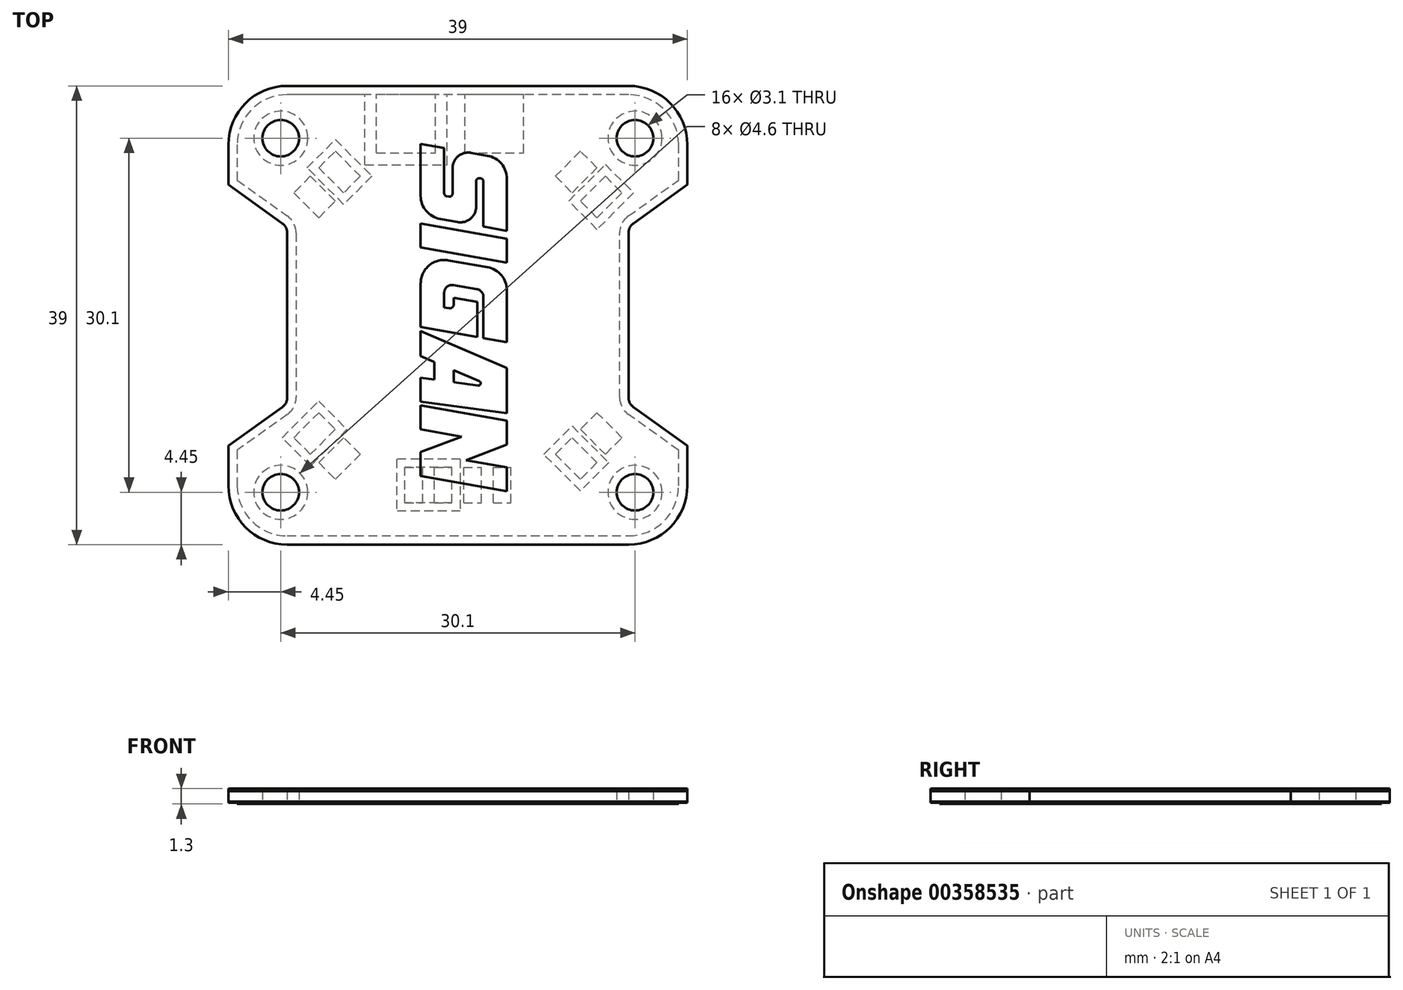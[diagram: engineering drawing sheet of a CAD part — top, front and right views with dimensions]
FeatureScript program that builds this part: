
annotation { "Feature Type Name" : "Feature", "Feature Type Description" : "" }
export const myFeature = defineFeature(function(context is Context, id is Id, definition is map)
    precondition{}
    {
        {
            var Q0;
            Q0=qCreatedBy(makeId("Top.planeOp"),FACE);
            var sketch = newSketch(context, id + "F0", { "sketchPlane" : qUnion([Q0])});
            skLineSegment(sketch, "E0.bottom", {"start": v(14.5, -19.5) * mm, "end": v(-14.5, -19.5) * mm});
            skLineSegment(sketch, "E0.top", {"start": v(14.5, 19.5) * mm, "end": v(7.5, 19.5) * mm});
            skLineSegment(sketch, "E0.left", {"start": v(19.5, -14.5) * mm, "end": v(19.5, -11.1) * mm});
            skLineSegment(sketch, "E0.right", {"start": v(-19.5, -14.5) * mm, "end": v(-19.5, -11.1) * mm});
            skPoint(sketch, "E0.middle", {"position": v(0, 0) * mm});
            skPoint(sketch, "E1.visualSharp", {"position": v(19.5, -19.5) * mm});
            skArc(sketch, "E1.filletArc", {"start": v(14.5, -19.5) * mm, "mid": v(18.04, -18.04) * mm, "end": v(19.5, -14.5) * mm});
            skPoint(sketch, "E2.visualSharp", {"position": v(-19.5, -19.5) * mm});
            skArc(sketch, "E2.filletArc", {"start": v(-19.5, -14.5) * mm, "mid": v(-18.04, -18.04) * mm, "end": v(-14.5, -19.5) * mm});
            skPoint(sketch, "E3.visualSharp", {"position": v(-19.5, 19.5) * mm});
            skArc(sketch, "E3.filletArc", {"start": v(-14.5, 19.5) * mm, "mid": v(-18.04, 18.04) * mm, "end": v(-19.5, 14.5) * mm});
            skPoint(sketch, "E4.visualSharp", {"position": v(19.5, 19.5) * mm});
            skArc(sketch, "E4.filletArc", {"start": v(19.5, 14.5) * mm, "mid": v(18.04, 18.04) * mm, "end": v(14.5, 19.5) * mm});
            skLineSegment(sketch, "E5", {"start": v(-7.5, 19.5) * mm, "end": v(-7.5, 19.5) * mm});
            skLineSegment(sketch, "E6", {"start": v(-7.5, 19.5) * mm, "end": v(7.5, 19.5) * mm});
            skLineSegment(sketch, "E7", {"start": v(7.5, 19.5) * mm, "end": v(7.5, 19.5) * mm});
            skLineSegment(sketch, "E8.trimOffspring", {"start": v(-7.5, 19.5) * mm, "end": v(-14.5, 19.5) * mm});
            skLineSegment(sketch, "E9", {"start": v(0, 19.5) * mm, "end": v(0, 0) * mm, "construction": true});
            skLineSegment(sketch, "E10.right", {"start": v(-14.5, 7) * mm, "end": v(-14.5, -7) * mm});
            skPoint(sketch, "E10.middle", {"position": v(-15.5, 0) * mm});
            skArc(sketch, "E11", {"start": v(-14.5, 7) * mm, "mid": v(-14.61, 7.46) * mm, "end": v(-14.92, 7.81) * mm});
            skArc(sketch, "E12", {"start": v(-14.92, -7.81) * mm, "mid": v(-14.61, -7.46) * mm, "end": v(-14.5, -7) * mm});
            skArc(sketch, "E13.MirrorCS", {"start": v(14.92, -7.81) * mm, "mid": v(14.61, -7.46) * mm, "end": v(14.5, -7) * mm});
            skArc(sketch, "E14.MirrorCS", {"start": v(14.5, 7) * mm, "mid": v(14.61, 7.46) * mm, "end": v(14.92, 7.81) * mm});
            skPoint(sketch, "E15.MirrorP", {"position": v(15.5, 0) * mm});
            skLineSegment(sketch, "E16.MirrorCS", {"start": v(14.5, 7) * mm, "end": v(14.5, -7) * mm});
            skCircle(sketch, "E17.0", {"center": v(-15.05, 15.05) * mm, "radius": 1.55 * mm});
            skCircle(sketch, "E17.1", {"center": v(15.05, 15.05) * mm, "radius": 1.55 * mm});
            skCircle(sketch, "E17.2", {"center": v(15.05, -15.05) * mm, "radius": 1.55 * mm});
            skCircle(sketch, "E17.3", {"center": v(-15.05, -15.05) * mm, "radius": 1.55 * mm});
            skLineSegment(sketch, "E18", {"start": v(14.92, -7.81) * mm, "end": v(19.5, -11.1) * mm});
            skLineSegment(sketch, "E19", {"start": v(0, 0) * mm, "end": v(26.56, 0) * mm, "construction": true});
            skLineSegment(sketch, "E20.MirrorCS", {"start": v(14.92, 7.81) * mm, "end": v(19.5, 11.1) * mm});
            skLineSegment(sketch, "E21.trimOffspring", {"start": v(19.5, 11.1) * mm, "end": v(19.5, 14.5) * mm});
            skPoint(sketch, "E22.orphan", {"position": v(16.5, 7) * mm});
            skPoint(sketch, "E23.MirrorCS.end.orphan", {"position": v(16.5, -7) * mm});
            skLineSegment(sketch, "E24.MirrorCS", {"start": v(-14.92, -7.81) * mm, "end": v(-19.5, -11.1) * mm});
            skLineSegment(sketch, "E25.MirrorCS", {"start": v(-14.92, 7.81) * mm, "end": v(-19.5, 11.1) * mm});
            skPoint(sketch, "E10.left.end.orphan", {"position": v(-16.5, -7) * mm});
            skPoint(sketch, "E26.orphan", {"position": v(-16.5, 7) * mm});
            skLineSegment(sketch, "E27.trimOffspring", {"start": v(-19.5, 11.1) * mm, "end": v(-19.5, 14.5) * mm});
            skSolve(sketch);
        }
        {
            var Q0;
            {var subQ0=makeQuery(id+"FaKBFoj8S7sMaQz_0.opExtrude","CAP_EDGE",EDGE,{"disambiguationData":[OSD([sQuery(id+"FUyg42RqR56omhc_0.wireOp",EDGE,"1f71cb04-1cd7-49c8-8af8-68a2ebdd6a70.filletArc")])],"isStart":true});Q0=makeQuery(id+"F0.imprint","IMPRINT",FACE,{"disambiguationData":[TD([[makeQuery(id+"F0.imprint","IMPRINT",EDGE,{"derivedFrom":subQ0}),-1.0]])]});}
            var Q1;
            Q1=makeQuery(id+"F0.imprint","IMPRINT",FACE,{"disambiguationData":[TD([[makeQuery(id+"F0.imprint","IMPRINT",EDGE,{"derivedFrom":sQuery(id+"F0.wireOp",EDGE,"E0.bottom")}),-1.0]])]});
            var Q2;
            {var subQ0=makeQuery(id+"FaKBFoj8S7sMaQz_0.opExtrude","CAP_EDGE",EDGE,{"disambiguationData":[OSD([sQuery(id+"FUyg42RqR56omhc_0.wireOp",EDGE,"45a09e78-3408-4181-94d1-7675ea45a7b5.0")])],"isStart":true});Q2=makeQuery(id+"F0.imprint","IMPRINT",FACE,{"disambiguationData":[TD([[makeQuery(id+"F0.imprint","IMPRINT",EDGE,{"derivedFrom":subQ0}),1.0]])]});}
            extrude(context, id + "F1", {"entities" : qUnion([Q0, Q1, Q2]), "depth" : 1 * mm});
        }
        {
            var Q0;
            Q0=makeQuery(id+"F1.opExtrude","SWEPT_BODY",BODY,{"disambiguationData":[OSD([sQuery(id+"FUyg42RqR56omhc_0.wireOp",EDGE,"apNCEg5n-BcgS-b9KA-570i-48yKU28l5lF8"),sQuery(id+"F0.wireOp",EDGE,"E0.bottom"),sQuery(id+"F0.wireOp",EDGE,"E0.top"),sQuery(id+"F0.wireOp",EDGE,"E0.left"),sQuery(id+"F0.wireOp",EDGE,"E0.right"),sQuery(id+"F0.wireOp",EDGE,"E1.filletArc"),sQuery(id+"F0.wireOp",EDGE,"E2.filletArc"),sQuery(id+"F0.wireOp",EDGE,"E3.filletArc"),sQuery(id+"F0.wireOp",EDGE,"E4.filletArc")])]});
            var Q1;
            Q1=qCreatedBy(makeId("Top.planeOp"),FACE);
            transform(context, id + "F2", {"entities" : qUnion([Q0]), "transformType" : TransformType.TRANSLATION_DISTANCE, "transformDirection" : qUnion([Q1]), "distance" : 6 * mm, "oppositeDirection" : true, "makeCopy" : false});
        }
        {
            var Q0;
            Q0=makeQuery(id+"F1.opExtrude","CAP_FACE",FACE,{"disambiguationData":[OSD([sQuery(id+"FUyg42RqR56omhc_0.wireOp",EDGE,"apNCEg5n-BcgS-b9KA-570i-48yKU28l5lF8"),sQuery(id+"F0.wireOp",EDGE,"E0.bottom"),sQuery(id+"F0.wireOp",EDGE,"E0.top"),sQuery(id+"F0.wireOp",EDGE,"E0.left"),sQuery(id+"F0.wireOp",EDGE,"E0.right"),sQuery(id+"F0.wireOp",EDGE,"E1.filletArc"),sQuery(id+"F0.wireOp",EDGE,"E2.filletArc"),sQuery(id+"F0.wireOp",EDGE,"E3.filletArc"),sQuery(id+"F0.wireOp",EDGE,"E4.filletArc"),sQuery(id+"F0.wireOp",EDGE,"E5"),sQuery(id+"F0.wireOp",EDGE,"E6"),sQuery(id+"F0.wireOp",EDGE,"E7"),sQuery(id+"F0.wireOp",EDGE,"E8.trimOffspring"),sQuery(id+"F0.wireOp",EDGE,"E10.left"),sQuery(id+"F0.wireOp",EDGE,"E10.right"),sQuery(id+"F0.wireOp",EDGE,"E11"),sQuery(id+"F0.wireOp",EDGE,"E12"),sQuery(id+"F0.wireOp",EDGE,"E13.MirrorCS"),sQuery(id+"F0.wireOp",EDGE,"E14.MirrorCS"),sQuery(id+"F0.wireOp",EDGE,"E23.MirrorCS"),sQuery(id+"F0.wireOp",EDGE,"E16.MirrorCS")])],"isStart":true});
            var sketch = newSketch(context, id + "F3", { "sketchPlane" : qUnion([Q0])});
            skLineSegment(sketch, "E28.bottom", {"start": v(0.6, -13.8) * mm, "end": v(5.6, -13.8) * mm});
            skLineSegment(sketch, "E28.top", {"start": v(0.6, -18.8) * mm, "end": v(5.6, -18.8) * mm});
            skLineSegment(sketch, "E28.left", {"start": v(0.6, -13.8) * mm, "end": v(0.6, -18.8) * mm});
            skLineSegment(sketch, "E28.right", {"start": v(5.6, -13.8) * mm, "end": v(5.6, -18.8) * mm});
            skPoint(sketch, "E28.middle", {"position": v(3.1, -16.3) * mm});
            skLineSegment(sketch, "E29.1.0.0", {"start": v(-1.9, -13.8) * mm, "end": v(-1.9, -18.8) * mm});
            skLineSegment(sketch, "E29.1.0.1", {"start": v(-6.9, -13.8) * mm, "end": v(-1.9, -13.8) * mm});
            skLineSegment(sketch, "E29.1.0.2", {"start": v(-6.9, -18.8) * mm, "end": v(-1.9, -18.8) * mm});
            skLineSegment(sketch, "E29.1.0.3", {"start": v(-6.9, -13.8) * mm, "end": v(-6.9, -18.8) * mm});
            skPoint(sketch, "E29.1.0.4", {"position": v(-4.4, -16.3) * mm});
            skLineSegment(sketch, "E29.direction1", {"start": v(0.6, -18.8) * mm, "end": v(-6.9, -18.8) * mm, "construction": true});
            skLineSegment(sketch, "E30", {"start": v(13.95, -10.41) * mm, "end": v(11.83, -8.29) * mm});
            skLineSegment(sketch, "E31", {"start": v(11.83, -8.29) * mm, "end": v(10.41, -9.7) * mm});
            skLineSegment(sketch, "E32", {"start": v(10.41, -9.7) * mm, "end": v(12.53, -11.83) * mm});
            skLineSegment(sketch, "E33", {"start": v(12.53, -11.83) * mm, "end": v(13.95, -10.41) * mm});
            skPoint(sketch, "E34.center", {"position": v(0, 0) * mm});
            skLineSegment(sketch, "E35", {"start": v(0, 0) * mm, "end": v(0, -24.64) * mm, "construction": true});
            skLineSegment(sketch, "E36", {"start": v(0, 0) * mm, "end": v(21.38, -21.38) * mm, "construction": true});
            skLineSegment(sketch, "E37.MirrorCS", {"start": v(8.29, -11.83) * mm, "end": v(9.7, -10.41) * mm});
            skLineSegment(sketch, "E38.MirrorCS", {"start": v(9.7, -10.41) * mm, "end": v(11.83, -12.53) * mm});
            skLineSegment(sketch, "E39.MirrorCS", {"start": v(10.41, -13.95) * mm, "end": v(8.29, -11.83) * mm});
            skLineSegment(sketch, "E40.MirrorCS", {"start": v(11.83, -12.53) * mm, "end": v(10.41, -13.95) * mm});
            skLineSegment(sketch, "E41.1.0", {"start": v(-8.29, -11.83) * mm, "end": v(-9.7, -10.41) * mm});
            skLineSegment(sketch, "E41.1.1", {"start": v(-11.83, -8.29) * mm, "end": v(-10.41, -9.7) * mm});
            skLineSegment(sketch, "E41.1.2", {"start": v(-10.41, -9.7) * mm, "end": v(-12.53, -11.83) * mm});
            skLineSegment(sketch, "E41.1.3", {"start": v(-9.7, -10.41) * mm, "end": v(-11.83, -12.53) * mm});
            skLineSegment(sketch, "E41.1.4", {"start": v(-11.83, -12.53) * mm, "end": v(-10.41, -13.95) * mm});
            skLineSegment(sketch, "E41.1.5", {"start": v(-12.53, -11.83) * mm, "end": v(-13.95, -10.41) * mm});
            skLineSegment(sketch, "E41.1.6", {"start": v(-10.41, -13.95) * mm, "end": v(-8.29, -11.83) * mm});
            skLineSegment(sketch, "E41.1.7", {"start": v(-13.95, -10.41) * mm, "end": v(-11.83, -8.29) * mm});
            skLineSegment(sketch, "E41.2.0", {"start": v(-11.83, 8.29) * mm, "end": v(-10.41, 9.7) * mm});
            skLineSegment(sketch, "E41.2.1", {"start": v(-8.29, 11.83) * mm, "end": v(-9.7, 10.41) * mm});
            skLineSegment(sketch, "E41.2.2", {"start": v(-9.7, 10.41) * mm, "end": v(-11.83, 12.53) * mm});
            skLineSegment(sketch, "E41.2.3", {"start": v(-10.41, 9.7) * mm, "end": v(-12.53, 11.83) * mm});
            skLineSegment(sketch, "E41.2.4", {"start": v(-12.53, 11.83) * mm, "end": v(-13.95, 10.41) * mm});
            skLineSegment(sketch, "E41.2.5", {"start": v(-11.83, 12.53) * mm, "end": v(-10.41, 13.95) * mm});
            skLineSegment(sketch, "E41.2.6", {"start": v(-13.95, 10.41) * mm, "end": v(-11.83, 8.29) * mm});
            skLineSegment(sketch, "E41.2.7", {"start": v(-10.41, 13.95) * mm, "end": v(-8.29, 11.83) * mm});
            skLineSegment(sketch, "E41.3.0", {"start": v(8.29, 11.83) * mm, "end": v(9.7, 10.41) * mm});
            skLineSegment(sketch, "E41.3.1", {"start": v(11.83, 8.29) * mm, "end": v(10.41, 9.7) * mm});
            skLineSegment(sketch, "E41.3.2", {"start": v(10.41, 9.7) * mm, "end": v(12.53, 11.83) * mm});
            skLineSegment(sketch, "E41.3.3", {"start": v(9.7, 10.41) * mm, "end": v(11.83, 12.53) * mm});
            skLineSegment(sketch, "E41.3.4", {"start": v(11.83, 12.53) * mm, "end": v(10.41, 13.95) * mm});
            skLineSegment(sketch, "E41.3.5", {"start": v(12.53, 11.83) * mm, "end": v(13.95, 10.41) * mm});
            skLineSegment(sketch, "E41.3.6", {"start": v(10.41, 13.95) * mm, "end": v(8.29, 11.83) * mm});
            skLineSegment(sketch, "E41.3.7", {"start": v(13.95, 10.41) * mm, "end": v(11.83, 8.29) * mm});
            skLineSegment(sketch, "E41.anchor1", {"start": v(0, 0) * mm, "end": v(10.41, -13.95) * mm, "construction": true});
            skLineSegment(sketch, "E41.anchor2", {"start": v(0, 0) * mm, "end": v(13.95, 10.41) * mm, "construction": true});
            skLineSegment(sketch, "E42.bottom", {"start": v(3, 15.94) * mm, "end": v(4.5, 15.94) * mm});
            skLineSegment(sketch, "E42.top", {"start": v(3, 12.94) * mm, "end": v(4.5, 12.94) * mm});
            skLineSegment(sketch, "E42.left", {"start": v(3, 15.94) * mm, "end": v(3, 12.94) * mm});
            skLineSegment(sketch, "E42.right", {"start": v(4.5, 15.94) * mm, "end": v(4.5, 12.94) * mm});
            skPoint(sketch, "E42.middle", {"position": v(3.75, 14.44) * mm});
            skPoint(sketch, "E43.1.0.0", {"position": v(1.25, 14.44) * mm});
            skLineSegment(sketch, "E43.1.0.1", {"start": v(0.5, 12.94) * mm, "end": v(2, 12.94) * mm});
            skLineSegment(sketch, "E43.1.0.2", {"start": v(2, 15.94) * mm, "end": v(2, 12.94) * mm});
            skLineSegment(sketch, "E43.1.0.3", {"start": v(0.5, 15.94) * mm, "end": v(0.5, 12.94) * mm});
            skLineSegment(sketch, "E43.1.0.4", {"start": v(0.5, 15.94) * mm, "end": v(2, 15.94) * mm});
            skPoint(sketch, "E43.2.0.0", {"position": v(-1.25, 14.44) * mm});
            skLineSegment(sketch, "E43.2.0.1", {"start": v(-2, 12.94) * mm, "end": v(-0.5, 12.94) * mm});
            skLineSegment(sketch, "E43.2.0.2", {"start": v(-0.5, 15.94) * mm, "end": v(-0.5, 12.94) * mm});
            skLineSegment(sketch, "E43.2.0.3", {"start": v(-2, 15.94) * mm, "end": v(-2, 12.94) * mm});
            skLineSegment(sketch, "E43.2.0.4", {"start": v(-2, 15.94) * mm, "end": v(-0.5, 15.94) * mm});
            skPoint(sketch, "E43.3.0.0", {"position": v(-3.75, 14.44) * mm});
            skLineSegment(sketch, "E43.3.0.1", {"start": v(-4.5, 12.94) * mm, "end": v(-3, 12.94) * mm});
            skLineSegment(sketch, "E43.3.0.2", {"start": v(-3, 15.94) * mm, "end": v(-3, 12.94) * mm});
            skLineSegment(sketch, "E43.3.0.3", {"start": v(-4.5, 15.94) * mm, "end": v(-4.5, 12.94) * mm});
            skLineSegment(sketch, "E43.3.0.4", {"start": v(-4.5, 15.94) * mm, "end": v(-3, 15.94) * mm});
            skLineSegment(sketch, "E43.direction1", {"start": v(3, 12.94) * mm, "end": v(0.5, 12.94) * mm, "construction": true});
            skSolve(sketch);
        }
        {
            var Q0;
            Q0=makeQuery(id+"F3.imprint","IMPRINT",FACE,{"disambiguationData":[TD([[makeQuery(id+"F3.imprint","IMPRINT",EDGE,{"derivedFrom":sQuery(id+"F3.wireOp",EDGE,"E28.bottom")}),1.0]])]});
            extrude(context, id + "F4", {"entities" : qUnion([Q0]), "depth" : .1 * mm});
        }
        {
            var Q0;
            Q0=makeQuery(id+"F1.opExtrude","CAP_FACE",FACE,{"disambiguationData":[OSD([sQuery(id+"FUyg42RqR56omhc_0.wireOp",EDGE,"apNCEg5n-BcgS-b9KA-570i-48yKU28l5lF8"),sQuery(id+"F0.wireOp",EDGE,"E0.bottom"),sQuery(id+"F0.wireOp",EDGE,"E0.top"),sQuery(id+"F0.wireOp",EDGE,"E0.left"),sQuery(id+"F0.wireOp",EDGE,"E0.right"),sQuery(id+"F0.wireOp",EDGE,"E1.filletArc"),sQuery(id+"F0.wireOp",EDGE,"E2.filletArc"),sQuery(id+"F0.wireOp",EDGE,"E3.filletArc"),sQuery(id+"F0.wireOp",EDGE,"E4.filletArc"),sQuery(id+"F0.wireOp",EDGE,"E5"),sQuery(id+"F0.wireOp",EDGE,"E6"),sQuery(id+"F0.wireOp",EDGE,"E7"),sQuery(id+"F0.wireOp",EDGE,"E8.trimOffspring"),sQuery(id+"F0.wireOp",EDGE,"E10.left"),sQuery(id+"F0.wireOp",EDGE,"E10.right"),sQuery(id+"F0.wireOp",EDGE,"E11"),sQuery(id+"F0.wireOp",EDGE,"E12"),sQuery(id+"F0.wireOp",EDGE,"E13.MirrorCS"),sQuery(id+"F0.wireOp",EDGE,"E14.MirrorCS"),sQuery(id+"F0.wireOp",EDGE,"E23.MirrorCS"),sQuery(id+"F0.wireOp",EDGE,"E16.MirrorCS")])],"isStart":true});
            var sketch = newSketch(context, id + "F5", { "sketchPlane" : qUnion([Q0])});
            skLineSegment(sketch, "E44.0", {"start": v(9.42, -9.7) * mm, "end": v(12.53, -12.82) * mm});
            skLineSegment(sketch, "E44.1", {"start": v(11.83, -7.3) * mm, "end": v(9.42, -9.7) * mm});
            skLineSegment(sketch, "E44.2", {"start": v(14.94, -10.41) * mm, "end": v(11.83, -7.3) * mm});
            skLineSegment(sketch, "E44.3", {"start": v(12.53, -12.82) * mm, "end": v(14.94, -10.41) * mm});
            skLineSegment(sketch, "E45.1.0", {"start": v(7.3, 11.83) * mm, "end": v(9.7, 9.42) * mm});
            skLineSegment(sketch, "E45.1.1", {"start": v(9.7, 9.42) * mm, "end": v(12.82, 12.53) * mm});
            skLineSegment(sketch, "E45.1.2", {"start": v(10.41, 14.94) * mm, "end": v(7.3, 11.83) * mm});
            skLineSegment(sketch, "E45.1.3", {"start": v(12.82, 12.53) * mm, "end": v(10.41, 14.94) * mm});
            skLineSegment(sketch, "E45.2.0", {"start": v(-11.83, 7.3) * mm, "end": v(-9.42, 9.7) * mm});
            skLineSegment(sketch, "E45.2.1", {"start": v(-9.42, 9.7) * mm, "end": v(-12.53, 12.82) * mm});
            skLineSegment(sketch, "E45.2.2", {"start": v(-14.94, 10.41) * mm, "end": v(-11.83, 7.3) * mm});
            skLineSegment(sketch, "E45.2.3", {"start": v(-12.53, 12.82) * mm, "end": v(-14.94, 10.41) * mm});
            skLineSegment(sketch, "E45.3.0", {"start": v(-7.3, -11.83) * mm, "end": v(-9.7, -9.42) * mm});
            skLineSegment(sketch, "E45.3.1", {"start": v(-9.7, -9.42) * mm, "end": v(-12.82, -12.53) * mm});
            skLineSegment(sketch, "E45.3.2", {"start": v(-10.41, -14.94) * mm, "end": v(-7.9, -12.43) * mm});
            skLineSegment(sketch, "E45.3.3", {"start": v(-12.82, -12.53) * mm, "end": v(-10.41, -14.94) * mm});
            skPoint(sketch, "E45.center", {"position": v(0, 0) * mm});
            skLineSegment(sketch, "E46.0", {"start": v(-0.9, -12.8) * mm, "end": v(-0.9, -19.5) * mm});
            skLineSegment(sketch, "E46.1", {"start": v(-7.9, -12.8) * mm, "end": v(-0.9, -12.8) * mm});
            skLineSegment(sketch, "E46.2", {"start": v(-7.9, -12.8) * mm, "end": v(-7.9, -19.5) * mm});
            skLineSegment(sketch, "E47.0", {"start": v(14.5, -19.5) * mm, "end": v(-14.5, -19.5) * mm});
            skLineSegment(sketch, "E48.trimOffspring", {"start": v(-7.9, -12.43) * mm, "end": v(-7.3, -11.83) * mm});
            skArc(sketch, "E49.0", {"start": v(18.75, -14.5) * mm, "mid": v(17.5, -17.5) * mm, "end": v(14.5, -18.75) * mm});
            skLineSegment(sketch, "E49.1", {"start": v(18.75, 14.5) * mm, "end": v(18.75, 11.48) * mm});
            skLineSegment(sketch, "E49.2", {"start": v(14.5, -18.75) * mm, "end": v(-14.5, -18.75) * mm});
            skArc(sketch, "E49.3", {"start": v(14.5, 18.75) * mm, "mid": v(17.5, 17.5) * mm, "end": v(18.75, 14.5) * mm});
            skArc(sketch, "E49.4", {"start": v(-14.5, -18.75) * mm, "mid": v(-17.5, -17.5) * mm, "end": v(-18.75, -14.5) * mm});
            skLineSegment(sketch, "E49.5", {"start": v(-18.75, 14.5) * mm, "end": v(-18.75, 11.48) * mm});
            skArc(sketch, "E49.6", {"start": v(-18.75, 14.5) * mm, "mid": v(-17.5, 17.5) * mm, "end": v(-14.5, 18.75) * mm});
            skLineSegment(sketch, "E49.7", {"start": v(14.5, 18.75) * mm, "end": v(-14.5, 18.75) * mm});
            skCircle(sketch, "E50.0", {"center": v(15.05, -15.05) * mm, "radius": 2.3 * mm});
            skCircle(sketch, "E51.0", {"center": v(-15.05, -15.05) * mm, "radius": 2.3 * mm});
            skCircle(sketch, "E52.0", {"center": v(-15.05, 15.05) * mm, "radius": 2.3 * mm});
            skCircle(sketch, "E53.0", {"center": v(15.05, 15.05) * mm, "radius": 2.3 * mm});
            skLineSegment(sketch, "E54.0", {"start": v(10.41, -9.7) * mm, "end": v(12.53, -11.83) * mm});
            skLineSegment(sketch, "E54.1", {"start": v(12.53, -11.83) * mm, "end": v(13.95, -10.41) * mm});
            skLineSegment(sketch, "E54.2", {"start": v(13.95, -10.41) * mm, "end": v(11.83, -8.29) * mm});
            skLineSegment(sketch, "E54.3", {"start": v(11.83, -8.29) * mm, "end": v(10.41, -9.7) * mm});
            skLineSegment(sketch, "E54.4", {"start": v(-10.41, -13.95) * mm, "end": v(-8.29, -11.83) * mm});
            skLineSegment(sketch, "E54.5", {"start": v(-11.83, -12.53) * mm, "end": v(-10.41, -13.95) * mm});
            skLineSegment(sketch, "E54.6", {"start": v(-9.7, -10.41) * mm, "end": v(-11.83, -12.53) * mm});
            skLineSegment(sketch, "E54.7", {"start": v(-8.29, -11.83) * mm, "end": v(-9.7, -10.41) * mm});
            skLineSegment(sketch, "E54.8", {"start": v(-13.95, 10.41) * mm, "end": v(-11.83, 8.29) * mm});
            skLineSegment(sketch, "E54.9", {"start": v(-11.83, 8.29) * mm, "end": v(-10.41, 9.7) * mm});
            skLineSegment(sketch, "E54.10", {"start": v(-12.53, 11.83) * mm, "end": v(-13.95, 10.41) * mm});
            skLineSegment(sketch, "E54.11", {"start": v(-10.41, 9.7) * mm, "end": v(-12.53, 11.83) * mm});
            skLineSegment(sketch, "E54.12", {"start": v(9.7, 10.41) * mm, "end": v(11.83, 12.53) * mm});
            skLineSegment(sketch, "E54.13", {"start": v(8.29, 11.83) * mm, "end": v(9.7, 10.41) * mm});
            skLineSegment(sketch, "E54.14", {"start": v(10.41, 13.95) * mm, "end": v(8.29, 11.83) * mm});
            skLineSegment(sketch, "E54.15", {"start": v(11.83, 12.53) * mm, "end": v(10.41, 13.95) * mm});
            skLineSegment(sketch, "E55.0", {"start": v(-1.9, -13.8) * mm, "end": v(-1.9, -18.8) * mm});
            skLineSegment(sketch, "E55.1", {"start": v(-6.9, -13.8) * mm, "end": v(-1.9, -13.8) * mm});
            skLineSegment(sketch, "E55.2", {"start": v(-6.9, -13.8) * mm, "end": v(-6.9, -18.8) * mm});
            skLineSegment(sketch, "E55.3", {"start": v(-6.9, -18.8) * mm, "end": v(-1.9, -18.8) * mm});
            skLineSegment(sketch, "E56.bottom", {"start": v(0.2, 12.24) * mm, "end": v(-5.2, 12.24) * mm});
            skLineSegment(sketch, "E56.top", {"start": v(0.2, 16.64) * mm, "end": v(-5.2, 16.64) * mm});
            skLineSegment(sketch, "E56.left", {"start": v(0.2, 12.24) * mm, "end": v(0.2, 16.64) * mm});
            skLineSegment(sketch, "E56.right", {"start": v(-5.2, 12.24) * mm, "end": v(-5.2, 16.64) * mm});
            skLineSegment(sketch, "E57.bottom", {"start": v(-0.5, 12.94) * mm, "end": v(-4.5, 12.94) * mm});
            skLineSegment(sketch, "E57.top", {"start": v(-0.5, 15.94) * mm, "end": v(-4.5, 15.94) * mm});
            skLineSegment(sketch, "E57.left", {"start": v(-0.5, 12.94) * mm, "end": v(-0.5, 15.94) * mm});
            skLineSegment(sketch, "E57.right", {"start": v(-4.5, 12.94) * mm, "end": v(-4.5, 15.94) * mm});
            skLineSegment(sketch, "E58.0", {"start": v(-14.48, 8.42) * mm, "end": v(-18.75, 11.48) * mm});
            skLineSegment(sketch, "E58.1", {"start": v(-14.48, -8.42) * mm, "end": v(-18.75, -11.48) * mm});
            skArc(sketch, "E58.2", {"start": v(-13.75, -7) * mm, "mid": v(-13.94, -7.8) * mm, "end": v(-14.48, -8.42) * mm});
            skLineSegment(sketch, "E58.3", {"start": v(-13.75, -7) * mm, "end": v(-13.75, 7) * mm});
            skArc(sketch, "E58.4", {"start": v(-14.48, 8.42) * mm, "mid": v(-13.94, 7.8) * mm, "end": v(-13.75, 7) * mm});
            skLineSegment(sketch, "E59.trimOffspring", {"start": v(-18.75, -11.48) * mm, "end": v(-18.75, -14.5) * mm});
            skLineSegment(sketch, "E60.0", {"start": v(14.48, 8.42) * mm, "end": v(18.75, 11.48) * mm});
            skLineSegment(sketch, "E60.1", {"start": v(14.48, -8.42) * mm, "end": v(18.75, -11.48) * mm});
            skArc(sketch, "E60.2", {"start": v(13.75, -7) * mm, "mid": v(13.94, -7.8) * mm, "end": v(14.48, -8.42) * mm});
            skLineSegment(sketch, "E60.3", {"start": v(13.75, -7) * mm, "end": v(13.75, 7) * mm});
            skArc(sketch, "E60.4", {"start": v(14.48, 8.42) * mm, "mid": v(13.94, 7.8) * mm, "end": v(13.75, 7) * mm});
            skLineSegment(sketch, "E61.trimOffspring", {"start": v(18.75, -11.48) * mm, "end": v(18.75, -14.5) * mm});
            skSolve(sketch);
        }
        {
            var Q0;
            Q0=makeQuery(id+"F5.imprint","IMPRINT",FACE,{"disambiguationData":[TD([[makeQuery(id+"F5.imprint","IMPRINT",EDGE,{"derivedFrom":sQuery(id+"F5.wireOp",EDGE,"E44.0")}),-1.0]])]});
            var Q1;
            Q1=makeQuery(id+"F5.imprint","IMPRINT",FACE,{"disambiguationData":[TD([[makeQuery(id+"F5.imprint","IMPRINT",EDGE,{"derivedFrom":sQuery(id+"F5.wireOp",EDGE,"E54.0")}),1.0]])]});
            var Q2;
            Q2=makeQuery(id+"F5.imprint","IMPRINT",FACE,{"disambiguationData":[TD([[makeQuery(id+"F5.imprint","IMPRINT",EDGE,{"derivedFrom":sQuery(id+"F5.wireOp",EDGE,"E54.4")}),1.0]])]});
            var Q3;
            Q3=makeQuery(id+"F5.imprint","IMPRINT",FACE,{"disambiguationData":[TD([[makeQuery(id+"F5.imprint","IMPRINT",EDGE,{"derivedFrom":sQuery(id+"F5.wireOp",EDGE,"E54.8")}),1.0]])]});
            var Q4;
            Q4=makeQuery(id+"F5.imprint","IMPRINT",FACE,{"disambiguationData":[TD([[makeQuery(id+"F5.imprint","IMPRINT",EDGE,{"derivedFrom":sQuery(id+"F5.wireOp",EDGE,"E54.12")}),1.0]])]});
            var Q5;
            {var subQ5=sQuery(id+"F5.wireOp",EDGE,"E55.1");Q5=makeQuery(id+"F5.imprint","IMPRINT",FACE,{"disambiguationData":[TD([[makeQuery(id+"F5.imprint","IMPRINT",EDGE,{"derivedFrom":subQ5}),-1.0]])]});}
            var Q6;
            Q6=makeQuery(id+"F5.imprint","IMPRINT",FACE,{"disambiguationData":[TD([[makeQuery(id+"F5.imprint","IMPRINT",EDGE,{"derivedFrom":sQuery(id+"F5.wireOp",EDGE,"E57.bottom")}),-1.0]])]});
            extrude(context, id + "F6", {"entities" : qUnion([Q0, Q1, Q2, Q3, Q4, Q5, Q6]), "depth" : .1 * mm});
        }
        {
            var Q0;
            Q0=makeQuery(id+"F4.opExtrude","SWEPT_BODY",BODY,{"disambiguationData":[OSD([sQuery(id+"FUyg42RqR56omhc_0.wireOp",EDGE,"apNCEg5n-BcgS-b9KA-570i-48yKU28l5lF8"),sQuery(id+"F0.wireOp",EDGE,"E0.bottom"),sQuery(id+"F0.wireOp",EDGE,"E0.top"),sQuery(id+"F0.wireOp",EDGE,"E0.left"),sQuery(id+"F0.wireOp",EDGE,"E0.right"),sQuery(id+"F0.wireOp",EDGE,"E1.filletArc"),sQuery(id+"F0.wireOp",EDGE,"E2.filletArc"),sQuery(id+"F0.wireOp",EDGE,"E3.filletArc"),sQuery(id+"F0.wireOp",EDGE,"E4.filletArc"),sQuery(id+"F0.wireOp",EDGE,"E5"),sQuery(id+"F0.wireOp",EDGE,"E6"),sQuery(id+"F0.wireOp",EDGE,"E7"),sQuery(id+"F0.wireOp",EDGE,"E8.trimOffspring"),sQuery(id+"F0.wireOp",EDGE,"E10.left"),sQuery(id+"F0.wireOp",EDGE,"E10.right"),sQuery(id+"F0.wireOp",EDGE,"E11"),sQuery(id+"F0.wireOp",EDGE,"E12"),sQuery(id+"F0.wireOp",EDGE,"E13.MirrorCS"),sQuery(id+"F0.wireOp",EDGE,"E14.MirrorCS"),sQuery(id+"F0.wireOp",EDGE,"E23.MirrorCS"),sQuery(id+"F0.wireOp",EDGE,"E16.MirrorCS"),sQuery(id+"F3.wireOp",EDGE,"E28.bottom"),sQuery(id+"F3.wireOp",EDGE,"E28.top"),sQuery(id+"F3.wireOp",EDGE,"E28.left"),sQuery(id+"F3.wireOp",EDGE,"E28.right"),sQuery(id+"F3.wireOp",EDGE,"E29.1.0.0"),sQuery(id+"F3.wireOp",EDGE,"E29.1.0.1"),sQuery(id+"F3.wireOp",EDGE,"E29.1.0.2"),sQuery(id+"F3.wireOp",EDGE,"E29.1.0.3"),sQuery(id+"F3.wireOp",EDGE,"E30"),sQuery(id+"F3.wireOp",EDGE,"E31"),sQuery(id+"F3.wireOp",EDGE,"E32"),sQuery(id+"F3.wireOp",EDGE,"E33"),sQuery(id+"F3.wireOp",EDGE,"E37.MirrorCS"),sQuery(id+"F3.wireOp",EDGE,"E38.MirrorCS"),sQuery(id+"F3.wireOp",EDGE,"E39.MirrorCS"),sQuery(id+"F3.wireOp",EDGE,"E40.MirrorCS"),sQuery(id+"F3.wireOp",EDGE,"E41.1.0"),sQuery(id+"F3.wireOp",EDGE,"E41.1.1"),sQuery(id+"F3.wireOp",EDGE,"E41.1.2"),sQuery(id+"F3.wireOp",EDGE,"E41.1.3"),sQuery(id+"F3.wireOp",EDGE,"E41.1.4"),sQuery(id+"F3.wireOp",EDGE,"E41.1.5"),sQuery(id+"F3.wireOp",EDGE,"E41.1.6"),sQuery(id+"F3.wireOp",EDGE,"E41.1.7"),sQuery(id+"F3.wireOp",EDGE,"E41.2.0"),sQuery(id+"F3.wireOp",EDGE,"E41.2.1"),sQuery(id+"F3.wireOp",EDGE,"E41.2.2"),sQuery(id+"F3.wireOp",EDGE,"E41.2.3"),sQuery(id+"F3.wireOp",EDGE,"E41.2.4"),sQuery(id+"F3.wireOp",EDGE,"E41.2.5"),sQuery(id+"F3.wireOp",EDGE,"E41.2.6"),sQuery(id+"F3.wireOp",EDGE,"E41.2.7"),sQuery(id+"F3.wireOp",EDGE,"E41.3.0"),sQuery(id+"F3.wireOp",EDGE,"E41.3.1"),sQuery(id+"F3.wireOp",EDGE,"E41.3.2"),sQuery(id+"F3.wireOp",EDGE,"E41.3.3"),sQuery(id+"F3.wireOp",EDGE,"E41.3.4"),sQuery(id+"F3.wireOp",EDGE,"E41.3.5"),sQuery(id+"F3.wireOp",EDGE,"E41.3.6"),sQuery(id+"F3.wireOp",EDGE,"E41.3.7"),sQuery(id+"F3.wireOp",EDGE,"E42.bottom"),sQuery(id+"F3.wireOp",EDGE,"E42.top"),sQuery(id+"F3.wireOp",EDGE,"E42.left"),sQuery(id+"F3.wireOp",EDGE,"E42.right"),sQuery(id+"F3.wireOp",EDGE,"E43.1.0.1"),sQuery(id+"F3.wireOp",EDGE,"E43.1.0.2"),sQuery(id+"F3.wireOp",EDGE,"E43.1.0.3"),sQuery(id+"F3.wireOp",EDGE,"E43.1.0.4"),sQuery(id+"F3.wireOp",EDGE,"E43.2.0.1"),sQuery(id+"F3.wireOp",EDGE,"E43.2.0.2"),sQuery(id+"F3.wireOp",EDGE,"E43.2.0.3"),sQuery(id+"F3.wireOp",EDGE,"E43.2.0.4"),sQuery(id+"F3.wireOp",EDGE,"E43.3.0.1"),sQuery(id+"F3.wireOp",EDGE,"E43.3.0.2"),sQuery(id+"F3.wireOp",EDGE,"E43.3.0.3"),sQuery(id+"F3.wireOp",EDGE,"E43.3.0.4")])]});
            var Q1;
            Q1=qCreatedBy(makeId("Top.planeOp"),FACE);
            transform(context, id + "F7", {"entities" : qUnion([Q0]), "transformType" : TransformType.TRANSLATION_DISTANCE, "transformDirection" : qUnion([Q1]), "distance" : .1 * mm, "makeCopy" : false});
        }
        {
            var Q0;
            Q0=makeQuery(id+"F1.opExtrude","CAP_FACE",FACE,{"disambiguationData":[OSD([sQuery(id+"FUyg42RqR56omhc_0.wireOp",EDGE,"apNCEg5n-BcgS-b9KA-570i-48yKU28l5lF8"),sQuery(id+"F0.wireOp",EDGE,"E0.bottom"),sQuery(id+"F0.wireOp",EDGE,"E0.top"),sQuery(id+"F0.wireOp",EDGE,"E0.left"),sQuery(id+"F0.wireOp",EDGE,"E0.right"),sQuery(id+"F0.wireOp",EDGE,"E1.filletArc"),sQuery(id+"F0.wireOp",EDGE,"E2.filletArc"),sQuery(id+"F0.wireOp",EDGE,"E3.filletArc"),sQuery(id+"F0.wireOp",EDGE,"E4.filletArc"),sQuery(id+"F0.wireOp",EDGE,"E6"),sQuery(id+"F0.wireOp",EDGE,"E8.trimOffspring"),sQuery(id+"F0.wireOp",EDGE,"E10.left"),sQuery(id+"F0.wireOp",EDGE,"E10.right"),sQuery(id+"F0.wireOp",EDGE,"E11"),sQuery(id+"F0.wireOp",EDGE,"E12"),sQuery(id+"F0.wireOp",EDGE,"E13.MirrorCS"),sQuery(id+"F0.wireOp",EDGE,"E14.MirrorCS"),sQuery(id+"F0.wireOp",EDGE,"E23.MirrorCS"),sQuery(id+"F0.wireOp",EDGE,"E16.MirrorCS")])],"isStart":false});
            var sketch = newSketch(context, id + "F8", { "sketchPlane" : qUnion([Q0])});
            skCircle(sketch, "E62.8", {"center": v(-15.05, -15.05) * mm, "radius": 2.3 * mm});
            skCircle(sketch, "E62.9", {"center": v(-15.05, 15.05) * mm, "radius": 2.3 * mm});
            skCircle(sketch, "E62.10", {"center": v(15.05, 15.05) * mm, "radius": 2.3 * mm});
            skCircle(sketch, "E62.11", {"center": v(15.05, -15.05) * mm, "radius": 2.3 * mm});
            skArc(sketch, "E63.0", {"start": v(18.75, 14.5) * mm, "mid": v(17.5, 17.5) * mm, "end": v(14.5, 18.75) * mm});
            skLineSegment(sketch, "E63.1", {"start": v(18.75, 11.48) * mm, "end": v(18.75, 14.5) * mm});
            skLineSegment(sketch, "E63.2", {"start": v(14.48, 8.42) * mm, "end": v(18.75, 11.48) * mm});
            skArc(sketch, "E63.3", {"start": v(13.75, 7) * mm, "mid": v(13.94, 7.8) * mm, "end": v(14.48, 8.42) * mm});
            skLineSegment(sketch, "E63.4", {"start": v(13.75, -7) * mm, "end": v(13.75, 7) * mm});
            skLineSegment(sketch, "E63.5", {"start": v(14.5, 18.75) * mm, "end": v(-14.5, 18.75) * mm});
            skArc(sketch, "E63.6", {"start": v(14.48, -8.42) * mm, "mid": v(13.94, -7.8) * mm, "end": v(13.75, -7) * mm});
            skLineSegment(sketch, "E63.7", {"start": v(18.75, -11.48) * mm, "end": v(14.48, -8.42) * mm});
            skLineSegment(sketch, "E63.8", {"start": v(18.75, -14.5) * mm, "end": v(18.75, -11.48) * mm});
            skArc(sketch, "E63.9", {"start": v(14.5, -18.75) * mm, "mid": v(17.5, -17.5) * mm, "end": v(18.75, -14.5) * mm});
            skArc(sketch, "E63.10", {"start": v(-14.48, 8.42) * mm, "mid": v(-13.94, 7.8) * mm, "end": v(-13.75, 7) * mm});
            skLineSegment(sketch, "E63.11", {"start": v(-18.75, 11.48) * mm, "end": v(-14.48, 8.42) * mm});
            skLineSegment(sketch, "E63.12", {"start": v(-18.75, 14.5) * mm, "end": v(-18.75, 11.48) * mm});
            skArc(sketch, "E63.13", {"start": v(-14.5, 18.75) * mm, "mid": v(-17.5, 17.5) * mm, "end": v(-18.75, 14.5) * mm});
            skLineSegment(sketch, "E63.14", {"start": v(-13.75, 7) * mm, "end": v(-13.75, -7) * mm});
            skArc(sketch, "E63.15", {"start": v(-13.75, -7) * mm, "mid": v(-13.94, -7.8) * mm, "end": v(-14.48, -8.42) * mm});
            skLineSegment(sketch, "E63.16", {"start": v(-14.48, -8.42) * mm, "end": v(-18.75, -11.48) * mm});
            skLineSegment(sketch, "E63.17", {"start": v(-18.75, -11.48) * mm, "end": v(-18.75, -14.5) * mm});
            skArc(sketch, "E63.18", {"start": v(-18.75, -14.5) * mm, "mid": v(-17.5, -17.5) * mm, "end": v(-14.5, -18.75) * mm});
            skLineSegment(sketch, "E63.19", {"start": v(-14.5, -18.75) * mm, "end": v(14.5, -18.75) * mm});
            skSolve(sketch);
        }
        {
            var Q0;
            Q0=qSketchRegion(id+"F8",true);
            extrude(context, id + "F9", {"entities" : qUnion([Q0]), "depth" : .1 * mm});
        }
        {
            var Q0;
            Q0=makeQuery(id+"F1.opExtrude","CAP_FACE",FACE,{"disambiguationData":[OSD([sQuery(id+"F0.wireOp",EDGE,"E0.bottom"),sQuery(id+"F0.wireOp",EDGE,"E0.top"),sQuery(id+"F0.wireOp",EDGE,"E0.left"),sQuery(id+"F0.wireOp",EDGE,"E0.right"),sQuery(id+"F0.wireOp",EDGE,"E1.filletArc"),sQuery(id+"F0.wireOp",EDGE,"E2.filletArc"),sQuery(id+"F0.wireOp",EDGE,"E3.filletArc"),sQuery(id+"F0.wireOp",EDGE,"E4.filletArc"),sQuery(id+"F0.wireOp",EDGE,"E6"),sQuery(id+"F0.wireOp",EDGE,"E8.trimOffspring"),sQuery(id+"F0.wireOp",EDGE,"E10.right"),sQuery(id+"F0.wireOp",EDGE,"E11"),sQuery(id+"F0.wireOp",EDGE,"E12"),sQuery(id+"F0.wireOp",EDGE,"E13.MirrorCS"),sQuery(id+"F0.wireOp",EDGE,"E14.MirrorCS"),sQuery(id+"F0.wireOp",EDGE,"E16.MirrorCS"),sQuery(id+"F0.wireOp",EDGE,"E17.0"),sQuery(id+"F0.wireOp",EDGE,"E17.1"),sQuery(id+"F0.wireOp",EDGE,"E17.2"),sQuery(id+"F0.wireOp",EDGE,"E17.3"),sQuery(id+"F0.wireOp",EDGE,"E18"),sQuery(id+"F0.wireOp",EDGE,"E20.MirrorCS"),sQuery(id+"F0.wireOp",EDGE,"E21.trimOffspring"),sQuery(id+"F0.wireOp",EDGE,"E24.MirrorCS"),sQuery(id+"F0.wireOp",EDGE,"E25.MirrorCS"),sQuery(id+"F0.wireOp",EDGE,"E27.trimOffspring")])],"isStart":false});
            extrude(context, id + "F10", {"entities" : qUnion([Q0]), "depth" : .1 * mm});
        }
        {
            var Q0;
            Q0=makeQuery(id+"F10.opExtrude","CAP_FACE",FACE,{"disambiguationData":[OSD([sQuery(id+"F0.wireOp",EDGE,"E0.bottom"),sQuery(id+"F0.wireOp",EDGE,"E0.top"),sQuery(id+"F0.wireOp",EDGE,"E0.left"),sQuery(id+"F0.wireOp",EDGE,"E0.right"),sQuery(id+"F0.wireOp",EDGE,"E1.filletArc"),sQuery(id+"F0.wireOp",EDGE,"E2.filletArc"),sQuery(id+"F0.wireOp",EDGE,"E3.filletArc"),sQuery(id+"F0.wireOp",EDGE,"E4.filletArc"),sQuery(id+"F0.wireOp",EDGE,"E6"),sQuery(id+"F0.wireOp",EDGE,"E8.trimOffspring"),sQuery(id+"F0.wireOp",EDGE,"E10.right"),sQuery(id+"F0.wireOp",EDGE,"E11"),sQuery(id+"F0.wireOp",EDGE,"E12"),sQuery(id+"F0.wireOp",EDGE,"E13.MirrorCS"),sQuery(id+"F0.wireOp",EDGE,"E14.MirrorCS"),sQuery(id+"F0.wireOp",EDGE,"E16.MirrorCS"),sQuery(id+"F0.wireOp",EDGE,"E17.0"),sQuery(id+"F0.wireOp",EDGE,"E17.1"),sQuery(id+"F0.wireOp",EDGE,"E17.2"),sQuery(id+"F0.wireOp",EDGE,"E17.3"),sQuery(id+"F0.wireOp",EDGE,"E18"),sQuery(id+"F0.wireOp",EDGE,"E20.MirrorCS"),sQuery(id+"F0.wireOp",EDGE,"E21.trimOffspring"),sQuery(id+"F0.wireOp",EDGE,"E24.MirrorCS"),sQuery(id+"F0.wireOp",EDGE,"E25.MirrorCS"),sQuery(id+"F0.wireOp",EDGE,"E27.trimOffspring")])],"isStart":false});
            var sketch = newSketch(context, id + "F11", { "sketchPlane" : qUnion([Q0])});
            skLineSegment(sketch, "E64.1.0", {"start": v(2.17, 1.56) * mm, "end": v(2.17, -1.95) * mm});
            skLineSegment(sketch, "E64.1.1", {"start": v(0.69, -12.32) * mm, "end": v(4.17, -12.93) * mm});
            skLineSegment(sketch, "E64.1.2", {"start": v(2.52, 4.09) * mm, "end": v(-0.81, 4.67) * mm});
            skPoint(sketch, "E64.1.3", {"position": v(2.17, 11.6) * mm});
            skPoint(sketch, "E64.1.4", {"position": v(1.55, 7.64) * mm});
            skPoint(sketch, "E64.1.5", {"position": v(2.17, 2.12) * mm});
            skLineSegment(sketch, "E64.1.6", {"start": v(4.17, -11) * mm, "end": v(0.69, -12.32) * mm});
            skPoint(sketch, "E64.1.7", {"position": v(3.14, -6.16) * mm});
            skLineSegment(sketch, "E64.1.8", {"start": v(4.17, -2.3) * mm, "end": v(4.17, 2.12) * mm});
            skPoint(sketch, "E64.1.9", {"position": v(-3.16, 5.09) * mm});
            skPoint(sketch, "E64.1.10", {"position": v(-3.16, 8.47) * mm});
            skLineSegment(sketch, "E64.1.11", {"start": v(0.32, -10.32) * mm, "end": v(-3.16, -9.7) * mm});
            skLineSegment(sketch, "E64.1.12", {"start": v(-3.16, 10.15) * mm, "end": v(-3.16, 14.56) * mm});
            skLineSegment(sketch, "E64.1.13", {"start": v(4.17, 7.18) * mm, "end": v(4.17, 11.6) * mm});
            skLineSegment(sketch, "E64.1.14", {"start": v(-3.16, -11.64) * mm, "end": v(0.32, -10.32) * mm});
            skLineSegment(sketch, "E64.1.15", {"start": v(4.17, -8.32) * mm, "end": v(-3.16, -7.34) * mm});
            skLineSegment(sketch, "E64.1.16", {"start": v(4.17, -8.96) * mm, "end": v(-3.16, -7.67) * mm});
            skLineSegment(sketch, "E64.1.17", {"start": v(-3.16, 5.76) * mm, "end": v(4.17, 4.47) * mm});
            skPoint(sketch, "E64.1.18", {"position": v(-1.16, 2.7) * mm});
            skPoint(sketch, "E64.1.19", {"position": v(-0.45, 14.09) * mm});
            skPoint(sketch, "E64.1.20", {"position": v(-1.16, 10.15) * mm});
            skPoint(sketch, "E64.1.21", {"position": v(-1.16, 0.67) * mm});
            skPoint(sketch, "E64.1.22", {"position": v(4.17, 3.8) * mm});
            skPoint(sketch, "E64.1.23", {"position": v(4.17, 13.27) * mm});
            skLineSegment(sketch, "E64.1.24", {"start": v(-3.16, -1.34) * mm, "end": v(4.17, -4.47) * mm});
            skLineSegment(sketch, "E64.1.25", {"start": v(4.17, -14.96) * mm, "end": v(-3.16, -13.67) * mm});
            skLineSegment(sketch, "E64.1.26", {"start": v(-3.16, -1) * mm, "end": v(1.65, -1.85) * mm});
            skPoint(sketch, "E64.1.27", {"position": v(-0.45, 10.03) * mm});
            skPoint(sketch, "E64.1.28", {"position": v(-3.16, -1) * mm});
            skLineSegment(sketch, "E64.1.29", {"start": v(-3.16, 2.7) * mm, "end": v(-3.16, -1) * mm});
            skPoint(sketch, "E64.1.30", {"position": v(-0.35, 0.53) * mm});
            skLineSegment(sketch, "E64.1.31", {"start": v(4.17, -4.47) * mm, "end": v(4.17, -8.32) * mm});
            skLineSegment(sketch, "E64.1.32", {"start": v(1.65, -1.85) * mm, "end": v(1.65, 1.13) * mm});
            skPoint(sketch, "E64.1.33", {"position": v(-3.16, 5.09) * mm});
            skPoint(sketch, "E64.1.34", {"position": v(1.55, 11.7) * mm});
            skLineSegment(sketch, "E64.1.35", {"start": v(-2, -5.47) * mm, "end": v(-2, -3.96) * mm});
            skArc(sketch, "E64.1.36", {"start": v(4.17, 2.12) * mm, "mid": v(3.7, 3.4) * mm, "end": v(2.52, 4.09) * mm});
            skArc(sketch, "E64.1.37", {"start": v(-0.02, 7.92) * mm, "mid": v(1.07, 8.2) * mm, "end": v(1.55, 9.23) * mm});
            skLineSegment(sketch, "E64.1.38", {"start": v(-3.16, -5.32) * mm, "end": v(-2, -5.47) * mm});
            skLineSegment(sketch, "E64.1.39", {"start": v(-3.16, -9.7) * mm, "end": v(-3.16, -7.67) * mm});
            skLineSegment(sketch, "E64.1.40", {"start": v(4.17, -8.96) * mm, "end": v(4.17, -11) * mm});
            skLineSegment(sketch, "E64.1.41", {"start": v(4.17, 4.47) * mm, "end": v(4.17, 6.5) * mm});
            skLineSegment(sketch, "E64.1.42", {"start": v(-3.16, -7.34) * mm, "end": v(-3.16, -5.32) * mm});
            skArc(sketch, "E64.1.43", {"start": v(4.17, 11.6) * mm, "mid": v(3.7, 12.88) * mm, "end": v(2.52, 13.56) * mm});
            skLineSegment(sketch, "E64.1.44", {"start": v(-1.16, 14.21) * mm, "end": v(-1.16, 10.37) * mm});
            skLineSegment(sketch, "E64.1.45", {"start": v(-3.16, 14.56) * mm, "end": v(-1.16, 14.21) * mm});
            skLineSegment(sketch, "E64.1.46", {"start": v(1.55, 11.39) * mm, "end": v(1.55, 9.23) * mm});
            skLineSegment(sketch, "E64.1.47", {"start": v(2.17, 7.53) * mm, "end": v(2.17, 11.37) * mm});
            skLineSegment(sketch, "E64.1.48", {"start": v(4.17, 7.18) * mm, "end": v(2.17, 7.53) * mm});
            skArc(sketch, "E64.1.49", {"start": v(-3.16, 10.15) * mm, "mid": v(-2.7, 8.86) * mm, "end": v(-1.5, 8.18) * mm});
            skLineSegment(sketch, "E64.1.50", {"start": v(-0.34, -5.7) * mm, "end": v(1.71, -5.97) * mm});
            skLineSegment(sketch, "E64.1.51", {"start": v(-3.16, -13.67) * mm, "end": v(-3.16, -11.64) * mm});
            skArc(sketch, "E64.1.52", {"start": v(-0.81, 4.67) * mm, "mid": v(-2.45, 4.24) * mm, "end": v(-3.16, 2.7) * mm});
            skLineSegment(sketch, "E64.1.53", {"start": v(1.82, -5.6) * mm, "end": v(-0.34, -4.67) * mm});
            skLineSegment(sketch, "E64.1.54", {"start": v(-0.34, -4.67) * mm, "end": v(-0.34, -5.7) * mm});
            skLineSegment(sketch, "E64.1.55", {"start": v(4.17, 6.5) * mm, "end": v(-3.16, 7.8) * mm});
            skLineSegment(sketch, "E64.1.56", {"start": v(-3.16, -3.47) * mm, "end": v(-3.16, -1.34) * mm});
            skLineSegment(sketch, "E64.1.57", {"start": v(2.17, -1.95) * mm, "end": v(4.17, -2.3) * mm});
            skLineSegment(sketch, "E64.1.58", {"start": v(4.17, -12.93) * mm, "end": v(4.17, -14.96) * mm});
            skLineSegment(sketch, "E64.1.59", {"start": v(-2, -3.96) * mm, "end": v(-3.16, -3.47) * mm});
            skArc(sketch, "E64.1.60", {"start": v(1.11, 13.81) * mm, "mid": v(0.03, 13.52) * mm, "end": v(-0.45, 12.5) * mm});
            skLineSegment(sketch, "E64.1.61", {"start": v(1.11, 13.81) * mm, "end": v(2.52, 13.56) * mm});
            skLineSegment(sketch, "E64.1.62", {"start": v(-0.45, 10.34) * mm, "end": v(-0.45, 12.5) * mm});
            skLineSegment(sketch, "E64.1.63", {"start": v(-0.02, 7.92) * mm, "end": v(-1.5, 8.18) * mm});
            skLineSegment(sketch, "E64.1.64", {"start": v(-3.16, 7.8) * mm, "end": v(-3.16, 5.76) * mm});
            skArc(sketch, "E64.1.65", {"start": v(1.71, -5.97) * mm, "mid": v(1.93, -5.83) * mm, "end": v(1.82, -5.6) * mm});
            skLineSegment(sketch, "E64.1.66", {"start": v(-0.38, 2.57) * mm, "end": v(1.62, 2.21) * mm});
            skLineSegment(sketch, "E64.1.67", {"start": v(1.65, 1.13) * mm, "end": v(-0.35, 1.48) * mm});
            skArc(sketch, "E64.1.68", {"start": v(2.17, 1.56) * mm, "mid": v(2.02, 1.99) * mm, "end": v(1.62, 2.21) * mm});
            skLineSegment(sketch, "E64.1.69", {"start": v(-1.16, 0.67) * mm, "end": v(-1.16, 1.9) * mm});
            skLineSegment(sketch, "E64.1.70", {"start": v(-0.74, 0.6) * mm, "end": v(-1.16, 0.67) * mm});
            skLineSegment(sketch, "E64.1.71", {"start": v(-0.35, 1.48) * mm, "end": v(-0.35, 0.93) * mm});
            skArc(sketch, "E64.1.72", {"start": v(-0.38, 2.57) * mm, "mid": v(-0.92, 2.42) * mm, "end": v(-1.16, 1.9) * mm});
            skArc(sketch, "E64.1.73", {"start": v(-0.74, 0.6) * mm, "mid": v(-0.47, 0.67) * mm, "end": v(-0.35, 0.93) * mm});
            skArc(sketch, "E64.1.74", {"start": v(-0.76, 10.08) * mm, "mid": v(-0.55, 10.14) * mm, "end": v(-0.45, 10.34) * mm});
            skLineSegment(sketch, "E64.1.75", {"start": v(-0.94, 10.11) * mm, "end": v(-0.76, 10.08) * mm});
            skLineSegment(sketch, "E64.1.76", {"start": v(1.95, 11.63) * mm, "end": v(1.86, 11.65) * mm});
            skArc(sketch, "E64.1.77", {"start": v(1.86, 11.65) * mm, "mid": v(1.64, 11.59) * mm, "end": v(1.55, 11.39) * mm});
            skArc(sketch, "E64.1.78", {"start": v(2.17, 11.37) * mm, "mid": v(2.1, 11.54) * mm, "end": v(1.95, 11.63) * mm});
            skArc(sketch, "E64.1.79", {"start": v(-1.16, 10.37) * mm, "mid": v(-1.1, 10.2) * mm, "end": v(-0.94, 10.11) * mm});
            skLineSegment(sketch, "E65.0", {"start": v(14.5, 19.5) * mm, "end": v(-14.5, 19.5) * mm});
            skArc(sketch, "E65.1", {"start": v(-14.5, 19.5) * mm, "mid": v(-18.04, 18.04) * mm, "end": v(-19.5, 14.5) * mm});
            skLineSegment(sketch, "E65.2", {"start": v(-19.5, -14.5) * mm, "end": v(-19.5, -11.1) * mm});
            skArc(sketch, "E65.3", {"start": v(-19.5, -14.5) * mm, "mid": v(-18.04, -18.04) * mm, "end": v(-14.5, -19.5) * mm});
            skLineSegment(sketch, "E65.4", {"start": v(14.5, -19.5) * mm, "end": v(-14.5, -19.5) * mm});
            skArc(sketch, "E65.5", {"start": v(14.5, -19.5) * mm, "mid": v(18.04, -18.04) * mm, "end": v(19.5, -14.5) * mm});
            skLineSegment(sketch, "E65.6", {"start": v(19.5, -14.5) * mm, "end": v(19.5, -11.1) * mm});
            skArc(sketch, "E65.7", {"start": v(19.5, 14.5) * mm, "mid": v(18.04, 18.04) * mm, "end": v(14.5, 19.5) * mm});
            skLineSegment(sketch, "E66.0", {"start": v(-14.92, -7.81) * mm, "end": v(-19.5, -11.1) * mm});
            skArc(sketch, "E66.1", {"start": v(-14.92, -7.81) * mm, "mid": v(-14.61, -7.46) * mm, "end": v(-14.5, -7) * mm});
            skLineSegment(sketch, "E66.2", {"start": v(-14.5, 7) * mm, "end": v(-14.5, -7) * mm});
            skArc(sketch, "E66.3", {"start": v(-14.5, 7) * mm, "mid": v(-14.61, 7.46) * mm, "end": v(-14.92, 7.81) * mm});
            skLineSegment(sketch, "E66.4", {"start": v(-14.92, 7.81) * mm, "end": v(-19.5, 11.1) * mm});
            skLineSegment(sketch, "E67.trimOffspring", {"start": v(-19.5, 11.1) * mm, "end": v(-19.5, 14.5) * mm});
            skLineSegment(sketch, "E68.0", {"start": v(14.92, -7.81) * mm, "end": v(19.5, -11.1) * mm});
            skArc(sketch, "E68.1", {"start": v(14.92, -7.81) * mm, "mid": v(14.61, -7.46) * mm, "end": v(14.5, -7) * mm});
            skLineSegment(sketch, "E68.2", {"start": v(14.5, 7) * mm, "end": v(14.5, -7) * mm});
            skArc(sketch, "E68.3", {"start": v(14.5, 7) * mm, "mid": v(14.61, 7.46) * mm, "end": v(14.92, 7.81) * mm});
            skLineSegment(sketch, "E68.4", {"start": v(14.92, 7.81) * mm, "end": v(19.5, 11.1) * mm});
            skLineSegment(sketch, "E69.trimOffspring", {"start": v(19.5, 11.1) * mm, "end": v(19.5, 14.5) * mm});
            skSolve(sketch);
        }
        {
            var Q0;
            Q0=makeQuery(id+"F11.imprint","IMPRINT",FACE,{"disambiguationData":[TD([[makeQuery(id+"F11.imprint","IMPRINT",EDGE,{"derivedFrom":sQuery(id+"F11.wireOp",EDGE,"E64.1.0")}),-1.0]])]});
            var Q1;
            Q1=makeQuery(id+"F11.imprint","IMPRINT",FACE,{"disambiguationData":[TD([[makeQuery(id+"F11.imprint","IMPRINT",EDGE,{"derivedFrom":sQuery(id+"F11.wireOp",EDGE,"E64.1.50")}),1.0]])]});
            extrude(context, id + "F12", {"entities" : qUnion([Q0, Q1]), "depth" : .1 * mm});
        }
        {
            var Q0;
            Q0=makeQuery(id+"F4.opExtrude","CAP_FACE",FACE,{"disambiguationData":[OSD([sQuery(id+"FUyg42RqR56omhc_0.wireOp",EDGE,"apNCEg5n-BcgS-b9KA-570i-48yKU28l5lF8"),sQuery(id+"F0.wireOp",EDGE,"E0.bottom"),sQuery(id+"F0.wireOp",EDGE,"E0.top"),sQuery(id+"F0.wireOp",EDGE,"E0.left"),sQuery(id+"F0.wireOp",EDGE,"E0.right"),sQuery(id+"F0.wireOp",EDGE,"E1.filletArc"),sQuery(id+"F0.wireOp",EDGE,"E2.filletArc"),sQuery(id+"F0.wireOp",EDGE,"E3.filletArc"),sQuery(id+"F0.wireOp",EDGE,"E4.filletArc"),sQuery(id+"F0.wireOp",EDGE,"E5"),sQuery(id+"F0.wireOp",EDGE,"E6"),sQuery(id+"F0.wireOp",EDGE,"E7"),sQuery(id+"F0.wireOp",EDGE,"E8.trimOffspring"),sQuery(id+"F0.wireOp",EDGE,"E10.left"),sQuery(id+"F0.wireOp",EDGE,"E10.right"),sQuery(id+"F0.wireOp",EDGE,"E11"),sQuery(id+"F0.wireOp",EDGE,"E12"),sQuery(id+"F0.wireOp",EDGE,"E13.MirrorCS"),sQuery(id+"F0.wireOp",EDGE,"E14.MirrorCS"),sQuery(id+"F0.wireOp",EDGE,"E23.MirrorCS"),sQuery(id+"F0.wireOp",EDGE,"E16.MirrorCS"),sQuery(id+"F3.wireOp",EDGE,"E28.bottom"),sQuery(id+"F3.wireOp",EDGE,"E28.top"),sQuery(id+"F3.wireOp",EDGE,"E28.left"),sQuery(id+"F3.wireOp",EDGE,"E28.right"),sQuery(id+"F3.wireOp",EDGE,"E29.1.0.0"),sQuery(id+"F3.wireOp",EDGE,"E29.1.0.1"),sQuery(id+"F3.wireOp",EDGE,"E29.1.0.2"),sQuery(id+"F3.wireOp",EDGE,"E29.1.0.3"),sQuery(id+"F3.wireOp",EDGE,"E30"),sQuery(id+"F3.wireOp",EDGE,"E31"),sQuery(id+"F3.wireOp",EDGE,"E32"),sQuery(id+"F3.wireOp",EDGE,"E33"),sQuery(id+"F3.wireOp",EDGE,"E37.MirrorCS"),sQuery(id+"F3.wireOp",EDGE,"E38.MirrorCS"),sQuery(id+"F3.wireOp",EDGE,"E39.MirrorCS"),sQuery(id+"F3.wireOp",EDGE,"E40.MirrorCS"),sQuery(id+"F3.wireOp",EDGE,"E41.1.0"),sQuery(id+"F3.wireOp",EDGE,"E41.1.1"),sQuery(id+"F3.wireOp",EDGE,"E41.1.2"),sQuery(id+"F3.wireOp",EDGE,"E41.1.3"),sQuery(id+"F3.wireOp",EDGE,"E41.1.4"),sQuery(id+"F3.wireOp",EDGE,"E41.1.5"),sQuery(id+"F3.wireOp",EDGE,"E41.1.6"),sQuery(id+"F3.wireOp",EDGE,"E41.1.7"),sQuery(id+"F3.wireOp",EDGE,"E41.2.0"),sQuery(id+"F3.wireOp",EDGE,"E41.2.1"),sQuery(id+"F3.wireOp",EDGE,"E41.2.2"),sQuery(id+"F3.wireOp",EDGE,"E41.2.3"),sQuery(id+"F3.wireOp",EDGE,"E41.2.4"),sQuery(id+"F3.wireOp",EDGE,"E41.2.5"),sQuery(id+"F3.wireOp",EDGE,"E41.2.6"),sQuery(id+"F3.wireOp",EDGE,"E41.2.7"),sQuery(id+"F3.wireOp",EDGE,"E41.3.0"),sQuery(id+"F3.wireOp",EDGE,"E41.3.1"),sQuery(id+"F3.wireOp",EDGE,"E41.3.2"),sQuery(id+"F3.wireOp",EDGE,"E41.3.3"),sQuery(id+"F3.wireOp",EDGE,"E41.3.4"),sQuery(id+"F3.wireOp",EDGE,"E41.3.5"),sQuery(id+"F3.wireOp",EDGE,"E41.3.6"),sQuery(id+"F3.wireOp",EDGE,"E41.3.7"),sQuery(id+"F3.wireOp",EDGE,"E42.bottom"),sQuery(id+"F3.wireOp",EDGE,"E42.top"),sQuery(id+"F3.wireOp",EDGE,"E42.left"),sQuery(id+"F3.wireOp",EDGE,"E42.right"),sQuery(id+"F3.wireOp",EDGE,"E43.1.0.1"),sQuery(id+"F3.wireOp",EDGE,"E43.1.0.2"),sQuery(id+"F3.wireOp",EDGE,"E43.1.0.3"),sQuery(id+"F3.wireOp",EDGE,"E43.1.0.4"),sQuery(id+"F3.wireOp",EDGE,"E43.2.0.1"),sQuery(id+"F3.wireOp",EDGE,"E43.2.0.2"),sQuery(id+"F3.wireOp",EDGE,"E43.2.0.3"),sQuery(id+"F3.wireOp",EDGE,"E43.2.0.4"),sQuery(id+"F3.wireOp",EDGE,"E43.3.0.1"),sQuery(id+"F3.wireOp",EDGE,"E43.3.0.2"),sQuery(id+"F3.wireOp",EDGE,"E43.3.0.3"),sQuery(id+"F3.wireOp",EDGE,"E43.3.0.4")])],"isStart":false});
            var sketch = newSketch(context, id + "F13", { "sketchPlane" : qUnion([Q0])});
            skLineSegment(sketch, "E70.0", {"start": v(7.5, -19.5) * mm, "end": v(7.5, -19.5) * mm});
            skLineSegment(sketch, "E70.1", {"start": v(7.5, -19.5) * mm, "end": v(14.5, -19.5) * mm});
            skLineSegment(sketch, "E70.2", {"start": v(14.5, -19.5) * mm, "end": v(7.5, -19.5) * mm});
            skArc(sketch, "E70.3", {"start": v(19.5, -14.5) * mm, "mid": v(18.04, -18.04) * mm, "end": v(14.5, -19.5) * mm});
            skLineSegment(sketch, "E70.4", {"start": v(19.5, 14.5) * mm, "end": v(19.5, -14.5) * mm});
            skArc(sketch, "E70.5", {"start": v(14.5, 19.5) * mm, "mid": v(18.04, 18.04) * mm, "end": v(19.5, 14.5) * mm});
            skLineSegment(sketch, "E70.6", {"start": v(14.5, 19.5) * mm, "end": v(-14.5, 19.5) * mm});
            skArc(sketch, "E70.7", {"start": v(-19.5, 14.5) * mm, "mid": v(-18.04, 18.04) * mm, "end": v(-14.5, 19.5) * mm});
            skLineSegment(sketch, "E70.8", {"start": v(-19.5, 14.5) * mm, "end": v(-19.5, 14.5) * mm});
            skArc(sketch, "E70.9", {"start": v(-14.5, -19.5) * mm, "mid": v(-18.04, -18.04) * mm, "end": v(-19.5, -14.5) * mm});
            skPoint(sketch, "E71.center", {"position": v(0, 0) * mm});
            skLineSegment(sketch, "E72.bottom", {"start": v(2.35, 12.93) * mm, "end": v(2.63, 12.93) * mm});
            skLineSegment(sketch, "E72.top", {"start": v(2.35, 11.9) * mm, "end": v(2.63, 11.9) * mm});
            skLineSegment(sketch, "E72.left", {"start": v(2.35, 12.93) * mm, "end": v(2.35, 12.55) * mm});
            skLineSegment(sketch, "E72.right", {"start": v(2.63, 12.93) * mm, "end": v(2.63, 12.55) * mm});
            skPoint(sketch, "E72.middle", {"position": v(2.5, 12.41) * mm});
            skLineSegment(sketch, "E73.bottom", {"start": v(3, 12.27) * mm, "end": v(2.63, 12.27) * mm});
            skLineSegment(sketch, "E73.top", {"start": v(3, 12.55) * mm, "end": v(2.63, 12.55) * mm});
            skLineSegment(sketch, "E73.left", {"start": v(3, 12.27) * mm, "end": v(3, 12.55) * mm});
            skLineSegment(sketch, "E73.right", {"start": v(1.98, 12.27) * mm, "end": v(1.98, 12.55) * mm});
            skLineSegment(sketch, "E74.bottom", {"start": v(-1.98, 12.27) * mm, "end": v(-3, 12.27) * mm});
            skLineSegment(sketch, "E74.top", {"start": v(-1.98, 12.55) * mm, "end": v(-3, 12.55) * mm});
            skLineSegment(sketch, "E74.left", {"start": v(-1.98, 12.27) * mm, "end": v(-1.98, 12.55) * mm});
            skLineSegment(sketch, "E74.right", {"start": v(-3, 12.27) * mm, "end": v(-3, 12.55) * mm});
            skPoint(sketch, "E74.middle", {"position": v(-2.5, 12.41) * mm});
            skPoint(sketch, "E74.middle.positionSnap0", {"position": v(1.98, 12.41) * mm});
            skPoint(sketch, "E74.centerSnap0", {"position": v(1.98, 12.41) * mm});
            skLineSegment(sketch, "E75.bottom", {"start": v(3.47, -12.47) * mm, "end": v(2.77, -12.47) * mm});
            skLineSegment(sketch, "E75.top", {"start": v(3.47, -9.84) * mm, "end": v(2.77, -9.84) * mm});
            skLineSegment(sketch, "E75.left", {"start": v(3.47, -12.47) * mm, "end": v(3.47, -11.5) * mm});
            skLineSegment(sketch, "E75.right", {"start": v(2.77, -12.47) * mm, "end": v(2.77, -11.5) * mm});
            skPoint(sketch, "E75.middle", {"position": v(3.12, -11.15) * mm});
            skLineSegment(sketch, "E76.bottom", {"start": v(4.44, -11.5) * mm, "end": v(3.47, -11.5) * mm});
            skLineSegment(sketch, "E76.top", {"start": v(4.44, -10.8) * mm, "end": v(3.47, -10.8) * mm});
            skLineSegment(sketch, "E76.left", {"start": v(4.44, -11.5) * mm, "end": v(4.44, -10.8) * mm});
            skLineSegment(sketch, "E76.right", {"start": v(1.8, -11.5) * mm, "end": v(1.8, -10.8) * mm});
            skLineSegment(sketch, "E77.bottom", {"start": v(-3.1, -11.5) * mm, "end": v(-5.72, -11.5) * mm});
            skLineSegment(sketch, "E77.top", {"start": v(-3.1, -10.8) * mm, "end": v(-5.72, -10.8) * mm});
            skLineSegment(sketch, "E77.left", {"start": v(-3.1, -11.5) * mm, "end": v(-3.1, -10.8) * mm});
            skLineSegment(sketch, "E77.right", {"start": v(-5.72, -11.5) * mm, "end": v(-5.72, -10.8) * mm});
            skPoint(sketch, "E77.middle", {"position": v(-4.4, -11.15) * mm});
            skPoint(sketch, "E77.middle.positionSnap0", {"position": v(1.8, -11.15) * mm});
            skPoint(sketch, "E77.middle.positionSnap1", {"position": v(-4.4, -13.8) * mm});
            skPoint(sketch, "E77.centerSnap0", {"position": v(1.8, -11.15) * mm});
            skPoint(sketch, "E77.centerSnap1", {"position": v(-4.4, -13.8) * mm});
            skLineSegment(sketch, "E78.trimOffspring", {"start": v(2.35, 12.55) * mm, "end": v(1.98, 12.55) * mm});
            skLineSegment(sketch, "E79.trimOffspring", {"start": v(2.63, 12.27) * mm, "end": v(2.63, 11.9) * mm});
            skLineSegment(sketch, "E80.trimOffspring", {"start": v(2.35, 12.27) * mm, "end": v(1.98, 12.27) * mm});
            skLineSegment(sketch, "E81.trimOffspring", {"start": v(2.35, 12.27) * mm, "end": v(2.35, 11.9) * mm});
            skLineSegment(sketch, "E82.trimOffspring", {"start": v(2.77, -11.5) * mm, "end": v(1.8, -11.5) * mm});
            skLineSegment(sketch, "E83.trimOffspring", {"start": v(2.77, -10.8) * mm, "end": v(2.77, -9.84) * mm});
            skLineSegment(sketch, "E84.trimOffspring", {"start": v(2.77, -10.8) * mm, "end": v(1.8, -10.8) * mm});
            skLineSegment(sketch, "E85.trimOffspring", {"start": v(3.47, -10.8) * mm, "end": v(3.47, -9.84) * mm});
            skLineSegment(sketch, "E86.bottom", {"start": v(8.36, -11.29) * mm, "end": v(7.66, -11.29) * mm});
            skLineSegment(sketch, "E86.top", {"start": v(8.36, -9.29) * mm, "end": v(7.66, -9.29) * mm});
            skLineSegment(sketch, "E86.left", {"start": v(8.36, -11.29) * mm, "end": v(8.36, -10.64) * mm});
            skLineSegment(sketch, "E86.right", {"start": v(7.66, -11.29) * mm, "end": v(7.66, -10.64) * mm});
            skPoint(sketch, "E86.middle", {"position": v(8, -10.29) * mm});
            skLineSegment(sketch, "E87.bottom", {"start": v(9, -10.64) * mm, "end": v(8.36, -10.64) * mm});
            skLineSegment(sketch, "E87.top", {"start": v(9, -9.94) * mm, "end": v(8.36, -9.94) * mm});
            skLineSegment(sketch, "E87.left", {"start": v(9, -10.64) * mm, "end": v(9, -9.94) * mm});
            skLineSegment(sketch, "E87.right", {"start": v(7, -10.64) * mm, "end": v(7, -9.94) * mm});
            skLineSegment(sketch, "E88.bottom", {"start": v(11.05, -8.53) * mm, "end": v(9.05, -8.53) * mm});
            skLineSegment(sketch, "E88.top", {"start": v(11.05, -7.83) * mm, "end": v(9.05, -7.83) * mm});
            skLineSegment(sketch, "E88.left", {"start": v(11.05, -8.53) * mm, "end": v(11.05, -7.83) * mm});
            skLineSegment(sketch, "E88.right", {"start": v(9.05, -8.53) * mm, "end": v(9.05, -7.83) * mm});
            skLineSegment(sketch, "E89.trimOffspring", {"start": v(7.66, -10.64) * mm, "end": v(7, -10.64) * mm});
            skLineSegment(sketch, "E90.trimOffspring", {"start": v(8.36, -9.94) * mm, "end": v(8.36, -9.29) * mm});
            skLineSegment(sketch, "E91.trimOffspring", {"start": v(7.66, -9.94) * mm, "end": v(7, -9.94) * mm});
            skLineSegment(sketch, "E92.trimOffspring", {"start": v(7.66, -9.94) * mm, "end": v(7.66, -9.29) * mm});
            skLineSegment(sketch, "E93.1.0", {"start": v(-9.94, -8.36) * mm, "end": v(-9.29, -8.36) * mm});
            skLineSegment(sketch, "E93.1.1", {"start": v(-9.29, -8.36) * mm, "end": v(-9.29, -7.66) * mm});
            skLineSegment(sketch, "E93.1.2", {"start": v(-9.94, -7.66) * mm, "end": v(-9.29, -7.66) * mm});
            skLineSegment(sketch, "E93.1.3", {"start": v(-8.53, -11.05) * mm, "end": v(-7.83, -11.05) * mm});
            skLineSegment(sketch, "E93.1.4", {"start": v(-11.29, -8.36) * mm, "end": v(-10.64, -8.36) * mm});
            skLineSegment(sketch, "E93.1.5", {"start": v(-11.29, -8.36) * mm, "end": v(-11.29, -7.66) * mm});
            skPoint(sketch, "E93.1.6", {"position": v(-10.29, -8) * mm});
            skLineSegment(sketch, "E93.1.7", {"start": v(-8.53, -11.05) * mm, "end": v(-8.53, -9.05) * mm});
            skLineSegment(sketch, "E93.1.8", {"start": v(-8.53, -9.05) * mm, "end": v(-7.83, -9.05) * mm});
            skLineSegment(sketch, "E93.1.9", {"start": v(-7.83, -11.05) * mm, "end": v(-7.83, -9.05) * mm});
            skLineSegment(sketch, "E93.1.10", {"start": v(-11.29, -7.66) * mm, "end": v(-10.64, -7.66) * mm});
            skPoint(sketch, "E93.1.11", {"position": v(-10.29, -8) * mm});
            skLineSegment(sketch, "E93.1.12", {"start": v(-9.94, -9) * mm, "end": v(-9.94, -8.36) * mm});
            skLineSegment(sketch, "E93.1.13", {"start": v(-10.64, -9) * mm, "end": v(-9.94, -9) * mm});
            skLineSegment(sketch, "E93.1.14", {"start": v(-10.64, -7) * mm, "end": v(-9.94, -7) * mm});
            skLineSegment(sketch, "E93.1.15", {"start": v(-10.64, -7.66) * mm, "end": v(-10.64, -7) * mm});
            skLineSegment(sketch, "E93.1.16", {"start": v(-9.94, -7.66) * mm, "end": v(-9.94, -7) * mm});
            skLineSegment(sketch, "E93.1.17", {"start": v(-10.64, -9) * mm, "end": v(-10.64, -8.36) * mm});
            skLineSegment(sketch, "E93.2.0", {"start": v(-8.36, 9.94) * mm, "end": v(-8.36, 9.29) * mm});
            skLineSegment(sketch, "E93.2.1", {"start": v(-8.36, 9.29) * mm, "end": v(-7.66, 9.29) * mm});
            skLineSegment(sketch, "E93.2.2", {"start": v(-7.66, 9.94) * mm, "end": v(-7.66, 9.29) * mm});
            skLineSegment(sketch, "E93.2.3", {"start": v(-11.05, 8.53) * mm, "end": v(-11.05, 7.83) * mm});
            skLineSegment(sketch, "E93.2.4", {"start": v(-8.36, 11.29) * mm, "end": v(-8.36, 10.64) * mm});
            skLineSegment(sketch, "E93.2.5", {"start": v(-8.36, 11.29) * mm, "end": v(-7.66, 11.29) * mm});
            skPoint(sketch, "E93.2.6", {"position": v(-8, 10.29) * mm});
            skLineSegment(sketch, "E93.2.7", {"start": v(-11.05, 8.53) * mm, "end": v(-9.05, 8.53) * mm});
            skLineSegment(sketch, "E93.2.8", {"start": v(-9.05, 8.53) * mm, "end": v(-9.05, 7.83) * mm});
            skLineSegment(sketch, "E93.2.9", {"start": v(-11.05, 7.83) * mm, "end": v(-9.05, 7.83) * mm});
            skLineSegment(sketch, "E93.2.10", {"start": v(-7.66, 11.29) * mm, "end": v(-7.66, 10.64) * mm});
            skPoint(sketch, "E93.2.11", {"position": v(-8, 10.29) * mm});
            skLineSegment(sketch, "E93.2.12", {"start": v(-9, 9.94) * mm, "end": v(-8.36, 9.94) * mm});
            skLineSegment(sketch, "E93.2.13", {"start": v(-9, 10.64) * mm, "end": v(-9, 9.94) * mm});
            skLineSegment(sketch, "E93.2.14", {"start": v(-7, 10.64) * mm, "end": v(-7, 9.94) * mm});
            skLineSegment(sketch, "E93.2.15", {"start": v(-7.66, 10.64) * mm, "end": v(-7, 10.64) * mm});
            skLineSegment(sketch, "E93.2.16", {"start": v(-7.66, 9.94) * mm, "end": v(-7, 9.94) * mm});
            skLineSegment(sketch, "E93.2.17", {"start": v(-9, 10.64) * mm, "end": v(-8.36, 10.64) * mm});
            skLineSegment(sketch, "E93.3.0", {"start": v(9.94, 8.36) * mm, "end": v(9.29, 8.36) * mm});
            skLineSegment(sketch, "E93.3.1", {"start": v(9.29, 8.36) * mm, "end": v(9.29, 7.66) * mm});
            skLineSegment(sketch, "E93.3.2", {"start": v(9.94, 7.66) * mm, "end": v(9.29, 7.66) * mm});
            skLineSegment(sketch, "E93.3.3", {"start": v(8.53, 11.05) * mm, "end": v(7.83, 11.05) * mm});
            skLineSegment(sketch, "E93.3.4", {"start": v(11.29, 8.36) * mm, "end": v(10.64, 8.36) * mm});
            skLineSegment(sketch, "E93.3.5", {"start": v(11.29, 8.36) * mm, "end": v(11.29, 7.66) * mm});
            skPoint(sketch, "E93.3.6", {"position": v(10.29, 8) * mm});
            skLineSegment(sketch, "E93.3.7", {"start": v(8.53, 11.05) * mm, "end": v(8.53, 9.05) * mm});
            skLineSegment(sketch, "E93.3.8", {"start": v(8.53, 9.05) * mm, "end": v(7.83, 9.05) * mm});
            skLineSegment(sketch, "E93.3.9", {"start": v(7.83, 11.05) * mm, "end": v(7.83, 9.05) * mm});
            skLineSegment(sketch, "E93.3.10", {"start": v(11.29, 7.66) * mm, "end": v(10.64, 7.66) * mm});
            skPoint(sketch, "E93.3.11", {"position": v(10.29, 8) * mm});
            skLineSegment(sketch, "E93.3.12", {"start": v(9.94, 9) * mm, "end": v(9.94, 8.36) * mm});
            skLineSegment(sketch, "E93.3.13", {"start": v(10.64, 9) * mm, "end": v(9.94, 9) * mm});
            skLineSegment(sketch, "E93.3.14", {"start": v(10.64, 7) * mm, "end": v(9.94, 7) * mm});
            skLineSegment(sketch, "E93.3.15", {"start": v(10.64, 7.66) * mm, "end": v(10.64, 7) * mm});
            skLineSegment(sketch, "E93.3.16", {"start": v(9.94, 7.66) * mm, "end": v(9.94, 7) * mm});
            skLineSegment(sketch, "E93.3.17", {"start": v(10.64, 9) * mm, "end": v(10.64, 8.36) * mm});
            skLineSegment(sketch, "E93.anchor1", {"start": v(0, 0) * mm, "end": v(7.66, -11.29) * mm, "construction": true});
            skLineSegment(sketch, "E93.anchor2", {"start": v(0, 0) * mm, "end": v(11.29, 7.66) * mm, "construction": true});
            skSolve(sketch);
        }
        {
            var Q0;
            Q0=makeQuery(id+"F13.imprint","IMPRINT",FACE,{"disambiguationData":[TD([[makeQuery(id+"F13.imprint","IMPRINT",EDGE,{"derivedFrom":makeQuery(id+"F4.opExtrude","CAP_EDGE",EDGE,{"disambiguationData":[OSD([sQuery(id+"F3.wireOp",EDGE,"E30")])],"isStart":false})}),1.0]])]});
            var Q1;
            {var subQ4=sQuery(id+"F13.wireOp",EDGE,"E70.2");Q1=makeQuery(id+"F13.imprint","IMPRINT",FACE,{"disambiguationData":[TD([[makeQuery(id+"F13.imprint","IMPRINT",EDGE,{"derivedFrom":subQ4}),-1.0]])]});}
            var Q2;
            Q2=makeQuery(id+"F13.imprint","IMPRINT",FACE,{"disambiguationData":[TD([[makeQuery(id+"F13.imprint","IMPRINT",EDGE,{"derivedFrom":makeQuery(id+"F4.opExtrude","CAP_EDGE",EDGE,{"disambiguationData":[OSD([sQuery(id+"F3.wireOp",EDGE,"E41.3.0")])],"isStart":false})}),1.0]])]});
            var Q3;
            Q3=makeQuery(id+"F13.imprint","IMPRINT",FACE,{"disambiguationData":[TD([[makeQuery(id+"F13.imprint","IMPRINT",EDGE,{"derivedFrom":makeQuery(id+"F4.opExtrude","CAP_EDGE",EDGE,{"disambiguationData":[OSD([sQuery(id+"F3.wireOp",EDGE,"E42.bottom")])],"isStart":false})}),-1.0]])]});
            var Q4;
            Q4=makeQuery(id+"F13.imprint","IMPRINT",FACE,{"disambiguationData":[TD([[makeQuery(id+"F13.imprint","IMPRINT",EDGE,{"derivedFrom":makeQuery(id+"F4.opExtrude","CAP_EDGE",EDGE,{"disambiguationData":[OSD([sQuery(id+"F3.wireOp",EDGE,"E43.1.0.1")])],"isStart":false})}),1.0]])]});
            var Q5;
            Q5=makeQuery(id+"F13.imprint","IMPRINT",FACE,{"disambiguationData":[TD([[makeQuery(id+"F13.imprint","IMPRINT",EDGE,{"derivedFrom":makeQuery(id+"F4.opExtrude","CAP_EDGE",EDGE,{"disambiguationData":[OSD([sQuery(id+"F3.wireOp",EDGE,"E43.2.0.1")])],"isStart":false})}),1.0]])]});
            var Q6;
            Q6=makeQuery(id+"F13.imprint","IMPRINT",FACE,{"disambiguationData":[TD([[makeQuery(id+"F13.imprint","IMPRINT",EDGE,{"derivedFrom":makeQuery(id+"F4.opExtrude","CAP_EDGE",EDGE,{"disambiguationData":[OSD([sQuery(id+"F3.wireOp",EDGE,"E41.2.1")])],"isStart":false})}),-1.0]])]});
            var Q7;
            Q7=makeQuery(id+"F13.imprint","IMPRINT",FACE,{"disambiguationData":[TD([[makeQuery(id+"F13.imprint","IMPRINT",EDGE,{"derivedFrom":makeQuery(id+"F4.opExtrude","CAP_EDGE",EDGE,{"disambiguationData":[OSD([sQuery(id+"F3.wireOp",EDGE,"E41.2.0")])],"isStart":false})}),1.0]])]});
            var Q8;
            Q8=makeQuery(id+"F13.imprint","IMPRINT",FACE,{"disambiguationData":[TD([[makeQuery(id+"F13.imprint","IMPRINT",EDGE,{"derivedFrom":makeQuery(id+"F4.opExtrude","CAP_EDGE",EDGE,{"disambiguationData":[OSD([sQuery(id+"F3.wireOp",EDGE,"E41.3.1")])],"isStart":false})}),-1.0]])]});
            var Q9;
            Q9=makeQuery(id+"F13.imprint","IMPRINT",FACE,{"disambiguationData":[TD([[makeQuery(id+"F13.imprint","IMPRINT",EDGE,{"derivedFrom":makeQuery(id+"F4.opExtrude","CAP_EDGE",EDGE,{"disambiguationData":[OSD([sQuery(id+"F3.wireOp",EDGE,"E37.MirrorCS")])],"isStart":false})}),-1.0]])]});
            var Q10;
            Q10=makeQuery(id+"F13.imprint","IMPRINT",FACE,{"disambiguationData":[TD([[makeQuery(id+"F13.imprint","IMPRINT",EDGE,{"derivedFrom":makeQuery(id+"F4.opExtrude","CAP_EDGE",EDGE,{"disambiguationData":[OSD([sQuery(id+"F3.wireOp",EDGE,"E28.bottom")])],"isStart":false})}),-1.0]])]});
            var Q11;
            Q11=makeQuery(id+"F13.imprint","IMPRINT",FACE,{"disambiguationData":[TD([[makeQuery(id+"F13.imprint","IMPRINT",EDGE,{"derivedFrom":makeQuery(id+"F4.opExtrude","CAP_EDGE",EDGE,{"disambiguationData":[OSD([sQuery(id+"F3.wireOp",EDGE,"E29.1.0.0")])],"isStart":false})}),-1.0]])]});
            var Q12;
            Q12=makeQuery(id+"F13.imprint","IMPRINT",FACE,{"disambiguationData":[TD([[makeQuery(id+"F13.imprint","IMPRINT",EDGE,{"derivedFrom":makeQuery(id+"F4.opExtrude","CAP_EDGE",EDGE,{"disambiguationData":[OSD([sQuery(id+"F3.wireOp",EDGE,"E41.1.0")])],"isStart":false})}),1.0]])]});
            var Q13;
            Q13=makeQuery(id+"F13.imprint","IMPRINT",FACE,{"disambiguationData":[TD([[makeQuery(id+"F13.imprint","IMPRINT",EDGE,{"derivedFrom":makeQuery(id+"F4.opExtrude","CAP_EDGE",EDGE,{"disambiguationData":[OSD([sQuery(id+"F3.wireOp",EDGE,"E41.1.1")])],"isStart":false})}),-1.0]])]});
            var Q14;
            Q14=makeQuery(id+"F13.imprint","IMPRINT",FACE,{"disambiguationData":[TD([[makeQuery(id+"F13.imprint","IMPRINT",EDGE,{"derivedFrom":makeQuery(id+"F4.opExtrude","CAP_EDGE",EDGE,{"disambiguationData":[OSD([sQuery(id+"F3.wireOp",EDGE,"E43.3.0.1")])],"isStart":false})}),1.0]])]});
            extrude(context, id + "F14", {"entities" : qUnion([Q0, Q1, Q2, Q3, Q4, Q5, Q6, Q7, Q8, Q9, Q10, Q11, Q12, Q13, Q14]), "depth" : .1 * mm});
        }
    });
